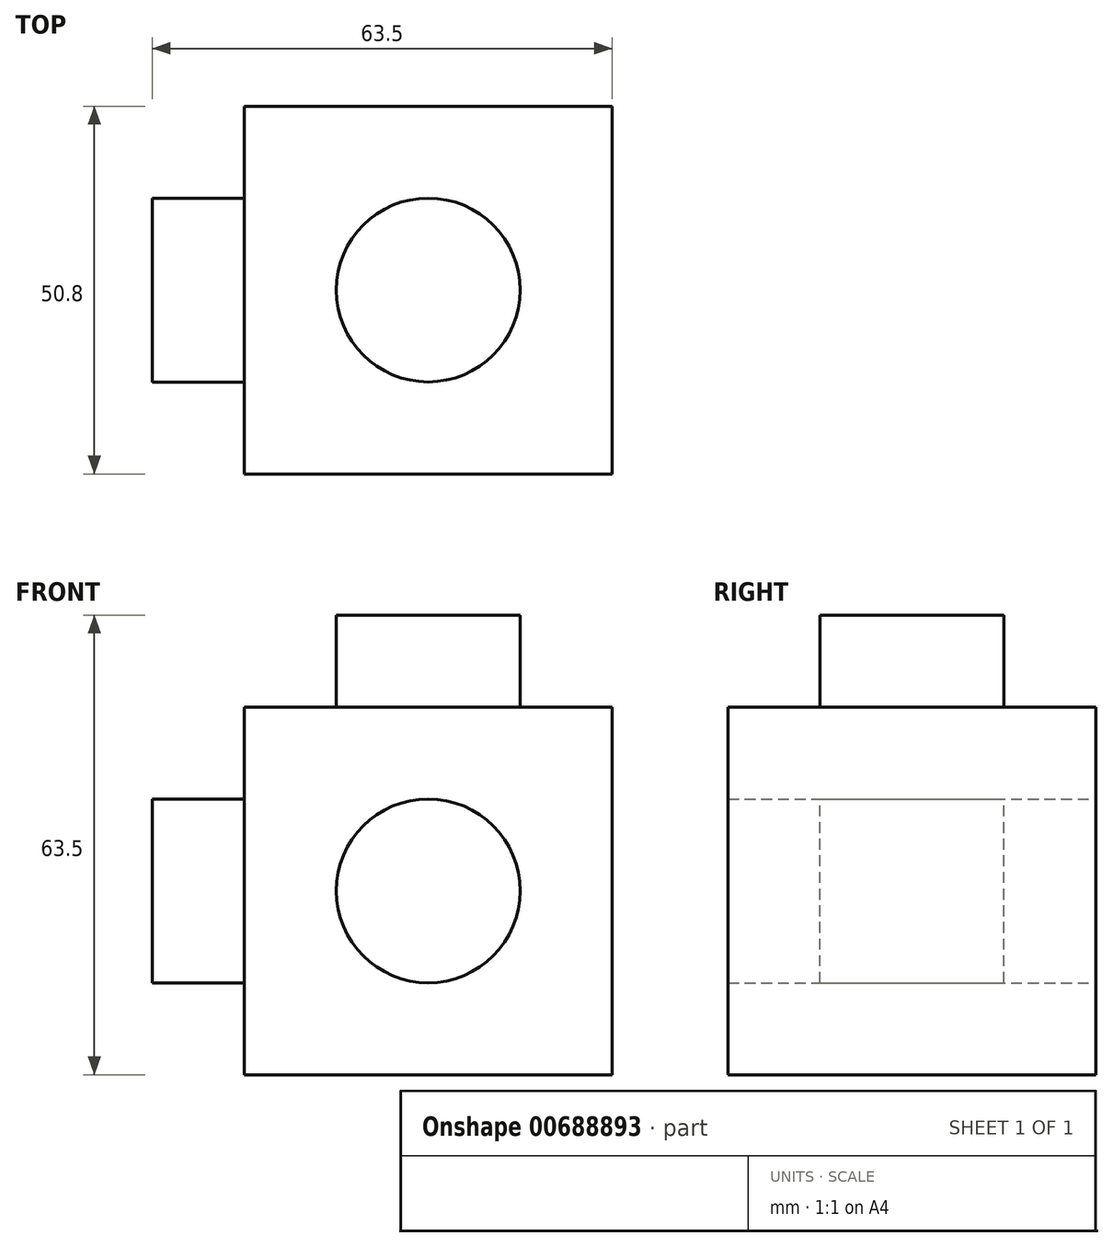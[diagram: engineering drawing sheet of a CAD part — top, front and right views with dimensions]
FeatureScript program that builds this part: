
annotation { "Feature Type Name" : "Feature", "Feature Type Description" : "" }
export const myFeature = defineFeature(function(context is Context, id is Id, definition is map)
    precondition{}
    {
        {
            var Q0;
            Q0=qCreatedBy(makeId("Front.planeOp"),FACE);
            var sketch = newSketch(context, id + "F0", { "sketchPlane" : qUnion([Q0])});
            skLineSegment(sketch, "E0.bottom", {"start": v(0, 0) * mm, "end": v(-50.8, 0) * mm});
            skLineSegment(sketch, "E0.top", {"start": v(0, 50.8) * mm, "end": v(-50.8, 50.8) * mm});
            skLineSegment(sketch, "E0.left", {"start": v(0, 0) * mm, "end": v(0, 50.8) * mm});
            skLineSegment(sketch, "E0.right", {"start": v(-50.8, 0) * mm, "end": v(-50.8, 50.8) * mm});
            skCircle(sketch, "E1", {"center": v(-25.4, 25.4) * mm, "radius": 12.7 * mm});
            skSolve(sketch);
        }
        {
            var Q0;
            Q0 = qSketchRegion(id + "F0", true);
            extrude(context, id + "F1", {"entities" : qUnion([Q0]), "depth" : 50.8 * mm, "offsetDistance" : 25.4 * mm});
        }
        {
            var Q0;
            Q0=makeQuery(id+"F1.opExtrude","SWEPT_FACE",FACE,{"disambiguationData":[OSD([sQuery(id+"F0.wireOp",EDGE,"E0.right")])]});
            var sketch = newSketch(context, id + "F2", { "sketchPlane" : qUnion([Q0])});
            skLineSegment(sketch, "E2.bottom", {"start": v(38.1, 12.7) * mm, "end": v(12.7, 12.7) * mm});
            skLineSegment(sketch, "E2.top", {"start": v(38.1, 38.1) * mm, "end": v(12.7, 38.1) * mm});
            skLineSegment(sketch, "E2.left", {"start": v(38.1, 12.7) * mm, "end": v(38.1, 38.1) * mm});
            skLineSegment(sketch, "E2.right", {"start": v(12.7, 12.7) * mm, "end": v(12.7, 38.1) * mm});
            skSolve(sketch);
        }
        {
            var Q0;
            Q0 = qSketchRegion(id + "F2", true);
            extrude(context, id + "F3", {"entities" : qUnion([Q0]), "operationType" : NewBodyOperationType.ADD, "depth" : 12.7 * mm, "offsetDistance" : 25.4 * mm});
        }
        {
            var Q0;
            Q0=makeQuery(id+"F1.opExtrude","SWEPT_FACE",FACE,{"disambiguationData":[OSD([sQuery(id+"F0.wireOp",EDGE,"E0.top")])]});
            var sketch = newSketch(context, id + "F4", { "sketchPlane" : qUnion([Q0])});
            skCircle(sketch, "E3", {"center": v(-25.4, -25.4) * mm, "radius": 12.7 * mm});
            skSolve(sketch);
        }
        {
            var Q0;
            Q0 = qSketchRegion(id + "F4", true);
            extrude(context, id + "F5", {"entities" : qUnion([Q0]), "operationType" : NewBodyOperationType.ADD, "depth" : 12.7 * mm, "offsetDistance" : 25.4 * mm});
        }
    });
